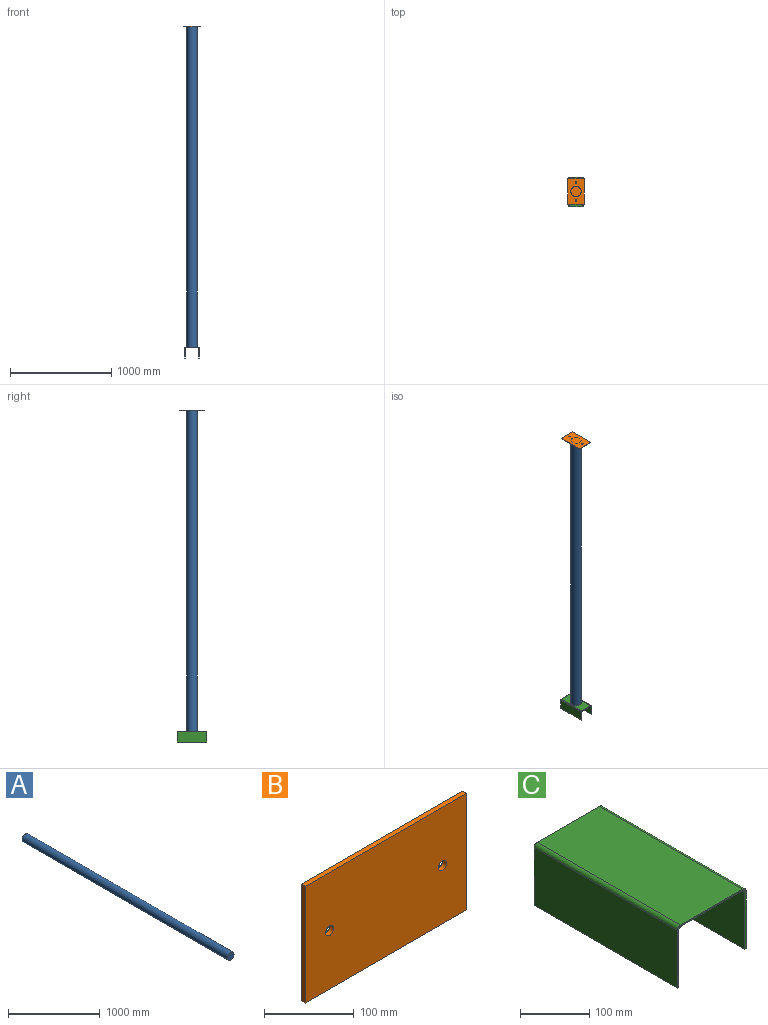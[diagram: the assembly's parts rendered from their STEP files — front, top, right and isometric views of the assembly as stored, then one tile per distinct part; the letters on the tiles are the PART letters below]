
ASSEMBLY  parts=3 mates=2
PART A: 3 faces, bbox 101.6x3166.3x101.6 mm
  f0: cylinder r=50.8mm len=3166.27mm, axis (0,1,0), area 1010628.1mm2, adj f1,f2
  f1: plane 101.6x101.6mm, normal (0,-1,0), area 8107.3mm2, adj f0
  f2: plane 101.6x101.6mm, normal (0,1,0), area 8107.3mm2, adj f0
PART B: 8 faces, bbox 254x6.4x158.8 mm
  f0: plane 254x6.35mm, normal (0,0,1), area 1612.9mm2, adj f1,f5,f6,f7
  f1: plane 158.75x6.35mm, normal (-1,0,0), area 1008.1mm2, adj f0,f2,f6,f7
  f2: plane 254x6.35mm, normal (0,0,-1), area 1612.9mm2, adj f1,f5,f6,f7
  f3: cylinder r=6.35mm len=12.7mm, axis (0,1,0), area 253.4mm2, adj f6,f7
  f4: cylinder r=6.35mm len=12.7mm, axis (0,1,0), area 253.4mm2, adj f6,f7
  f5: plane 158.75x6.35mm, normal (1,0,0), area 1008.1mm2, adj f0,f2,f6,f7
  f6: plane 254x158.75mm, normal (0,-1,0), area 40069.1mm2, adj f0,f1,f2,f3,f4,f5
  f7: plane 254x158.75mm, normal (0,1,0), area 40069.1mm2, adj f0,f1,f2,f3,f4,f5
PART C: 14 faces, bbox 139.7x292.1x108 mm
  f0: plane 292.1x101.6mm, normal (-1,0,0), area 29677.4mm2, adj f1,f11,f12,f13
  f1: plane 292.1x2.38mm, normal (0,0,-1), area 695.6mm2, adj f0,f2,f12,f13
  f2: plane 292.1x99.22mm, normal (1,0,0), area 28981.8mm2, adj f1,f3,f12,f13
  f3: cylinder r=6.35mm len=292.1mm, axis (0,1,0), area 2913.6mm2, adj f2,f4,f12,f13
  f4: plane 292.1x122.24mm, normal (0,0,-1), area 35705.6mm2, adj f3,f5,f12,f13
  f5: cylinder r=6.35mm len=292.1mm, axis (0,1,0), area 2913.6mm2, adj f4,f6,f12,f13
  f6: plane 292.1x99.22mm, normal (-1,0,0), area 28981.8mm2, adj f5,f7,f12,f13
  f7: plane 292.1x2.38mm, normal (0,0,-1), area 695.6mm2, adj f6,f8,f12,f13
  f8: plane 292.1x101.6mm, normal (1,0,0), area 29677.4mm2, adj f7,f9,f12,f13
  f9: cylinder r=6.35mm len=292.1mm, axis (0,1,0), area 2913.6mm2, adj f8,f10,f12,f13
  f10: plane 292.1x127mm, normal (0,0,1), area 37096.7mm2, adj f9,f11,f12,f13
  f11: cylinder r=6.35mm len=292.1mm, axis (0,1,0), area 2913.6mm2, adj f0,f10,f12,f13
  f12: plane 139.7x107.95mm, normal (0,-1,0), area 835.4mm2, adj f0,f1,f2,f3,f4,f5,f6,f7
  f13: plane 139.7x107.95mm, normal (0,1,0), area 835.4mm2, adj f0,f1,f2,f3,f4,f5,f6,f7
PLACE A rot(axis=(1,0,0),90deg) t=(-887.28,-419.93,3163.29)mm
PLACE B rot(axis=(0.58,0.58,0.58),120deg) t=(-399.28,-205.1,3169.64)mm
PLACE C t=(-107.27,-273.88,537.33)mm
MATE fastened B.f6 <-> A.f0  axis (0,0,-1) through (-662.49,-419.93,3163.29)mm
MATE fastened A.f0 <-> C.f10  axis (0,0,-1) through (-662.49,-419.93,-2.97)mm
